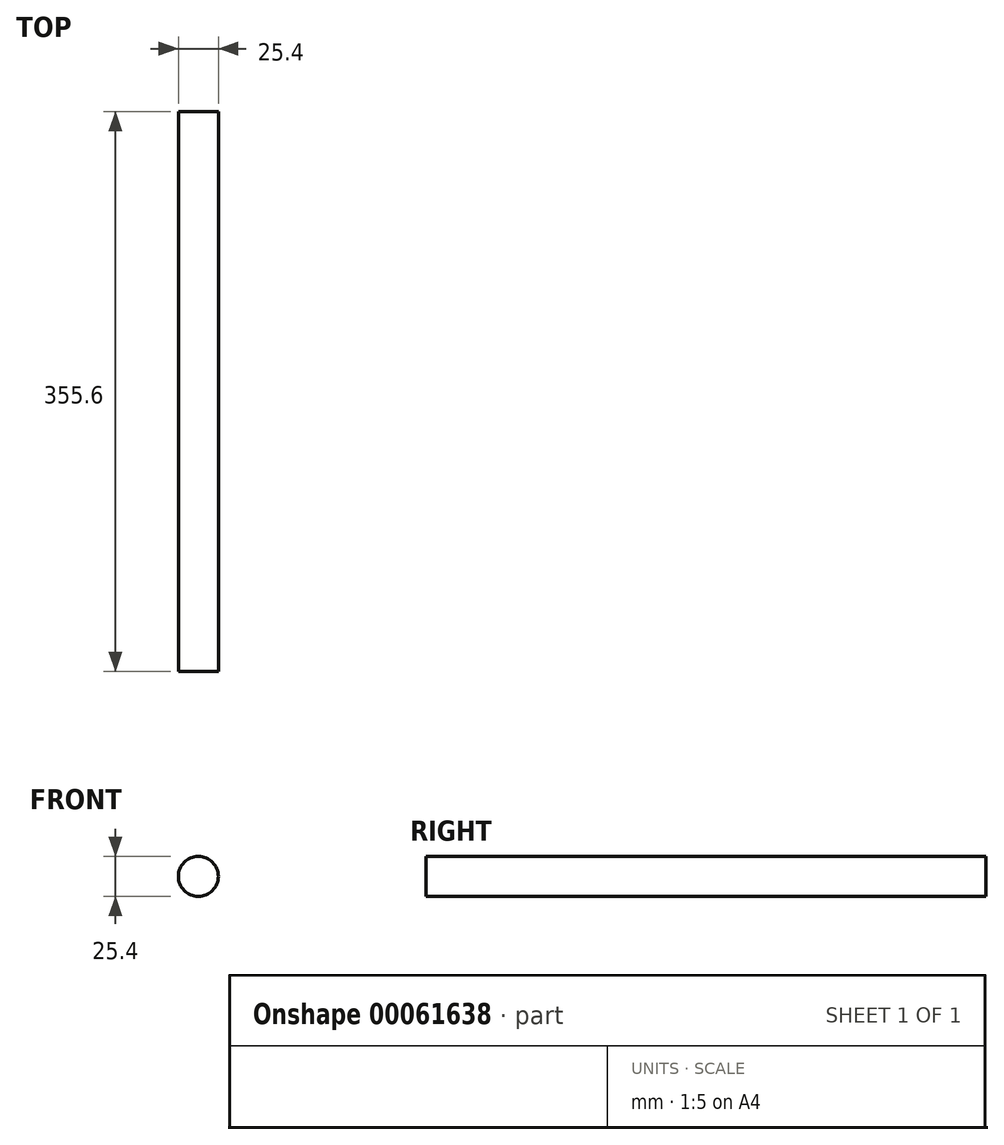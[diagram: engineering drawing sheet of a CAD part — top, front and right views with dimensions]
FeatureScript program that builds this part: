
annotation { "Feature Type Name" : "Feature", "Feature Type Description" : "" }
export const myFeature = defineFeature(function(context is Context, id is Id, definition is map)
    precondition{}
    {
        {
            var Q0;
            Q0=qCreatedBy(makeId("Front.planeOp"),FACE);
            var sketch = newSketch(context, id + "F0", { "sketchPlane" : qUnion([Q0])});
            skCircle(sketch, "E0", {"center": v(-21.99, 11.21) * mm, "radius": 12.7 * mm});
            skSolve(sketch);
        }
        {
            var Q0;
            Q0=makeQuery(id+"F0.imprint","IMPRINT",FACE,{"disambiguationData":[TD([[makeQuery(id+"F0.imprint","IMPRINT",EDGE,{"derivedFrom":sQuery(id+"F0.wireOp",EDGE,"E0")}),1.0]])]});
            extrude(context, id + "F1", {"entities" : qUnion([Q0]), "depth" : 355.6 * mm});
        }
    });
